# Revit family: LUXI_PANEL LIGHT_IP
name_source: partatom
category: Apparecchi per illuminazione
revit_build: Autodesk Revit 2016 (Build: 20161004_0715(x64)
units: mm (PartAtom-declared; Revit-internal decimal feet)

## family parameters
Condiviso = No
Host = Superficie
Numero OmniClass = 23.80.70.00
Punto di calcolo locali = Sì
Quota connettore circolare = Usa diametro
Sorgente d'illuminazione = Sì
Taglio con vuoti quando caricato = No
Tipo di parte = Normale
Titolo OmniClass = Lighting

## types (1)
- LPIP036660W840D
    Angolo inclinazione = -90.00°
    CRI = ≥80 (typ.)
    Carico apparente = 36 VA
    Certifications = CE / RohS
    Code = LPIP036660W840D
    Color = White
    Descrizione = LED panel, high protection rating
    Dimming = 1-10V / DALI / PUSH DIM
    Dust and water protection rating = IP65
    Emetti da larghezza rettangolo = 519 mm  [stored 1.70276 ft]
    Emetti da lunghezza rettangolo = 519 mm  [stored 1.70276 ft]
    Energy class = A+
    File diagramma fotometrico = LPIP036660W840D Luxi Serie IP 36W 595x595 4000K IP65.IES
    Filtro dei colori = 16777215
    H = 15 mm  [stored 0.0492126 ft]
    IFCExportAs = IFCLightFixtureType
    Impact rating = IK06 (1 Joule)
    Installation = Recessed / ceiling / suspended
    Length = 595 mm  [stored 1.9521 ft]
    Lifetime = L70B20 60.000h
    Light distribution = Edge light
    Light source = LED SMD
    Masterformat 2016 code = 26.50.00
    Masterformat 2016 description = Lighting
    Material 1 = High Trasmittance Opal Technopolimer
    Material 2 = Extruded Aluminum_White
    Material 3 = Sheet Steel
    Modello = IP Series | Panel Light
    OFF1 = 38 mm  [stored 0.124672 ft]
    OFF2 = 4 mm  [stored 0.0131234 ft]
    OFF3 = 11 mm  [stored 0.0360892 ft]
    Operating temperature = 0°C / +40°C
    Optics = Opal diffusing panel
    Photobiological risk group = RG0
    Power factor = ≥0,95 (typ.)
    Power supply = Included, dimmable
    Produttore = Luxi Illuminazione S.r.l.
    Prospetto di default = 2000 mm  [stored 6.56168 ft]
    Protection class = II
    Rated supply voltage = 220-240V AC / 50-60 Hz
    Rendi la forma visibile nel rendering = No
    Review = 3
    Size = 595x595x11
    Step MacAdam (SDCM) = <4
    URL = https://www.luxi.lighting
    Uniclass 2015 code = EF_70_80
    Uniclass 2015 description = Lighting
    Variazione temperatura colore lampada con luminosità attenuata = <Nessuno>
    Warranty = 5 years
    Wattage = 36 W
    Weight = 3.20 kg
    Width = 595 mm  [stored 1.9521 ft]

note: [stored X ft] marks values corroborated as IEEE doubles in the binary element streams (Revit-internal decimal feet)
